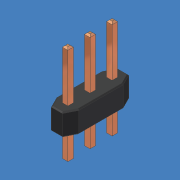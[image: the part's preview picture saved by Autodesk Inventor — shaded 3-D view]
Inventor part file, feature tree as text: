
AUTODESK INVENTOR PART (.ipt)
format: ipt  version: 2011 SP1 (Build 150282100, 282)  size: 181,248 bytes
history: native  units: mm (DEFAULTED — no unit token found)
features: chamfer x6, extrude x2, sketch x2, plane x1
ambient origin geometry x8: Origin, YZ Plane, XZ Plane, XY Plane, X Axis, Y Axis, Z Axis, Center Point
bodies: Solid1 (feature_tree)
feature tree (11):
  extrude  "Extrusion1"  Depth=7.62mm
  chamfer  "Chamfer1"  Distance=2.54mm
  chamfer  "Chamfer2"  Distance=0.9525mm
  chamfer  "Chamfer3"  Distance=2.54mm
  chamfer  "Chamfer4"  Distance=1.27mm
  plane  "Work Plane1"
  sketch  "Sketch2"  dims[d5=0.635mm d6=2.54mm d7=0.9525mm d8=2.54mm d9=0.0mm d10=1.27mm d11=0.635mm d12=1.27mm d13=0.635mm d14=1.27mm d15=0.635mm d16=1.27mm d17=0.635mm d18=3.175mm d19=11.43mm d20=0.0mm d21=0.1778mm d22=0.635mm d23=0.127mm d24=0.635mm d25=2.54mm d26=45.0deg d27=45.0deg d28=45.0deg d29=45.0deg d30=45.0deg d31=45.0deg]
  extrude  "Extrusion2"  Depth=1.27mm
  chamfer  "Chamfer5"  Distance=1.27mm
  chamfer  "Chamfer6"  Distance=1.27mm
  sketch  "Sketch1"  dims[d3=2.54mm d4=7.62mm]
